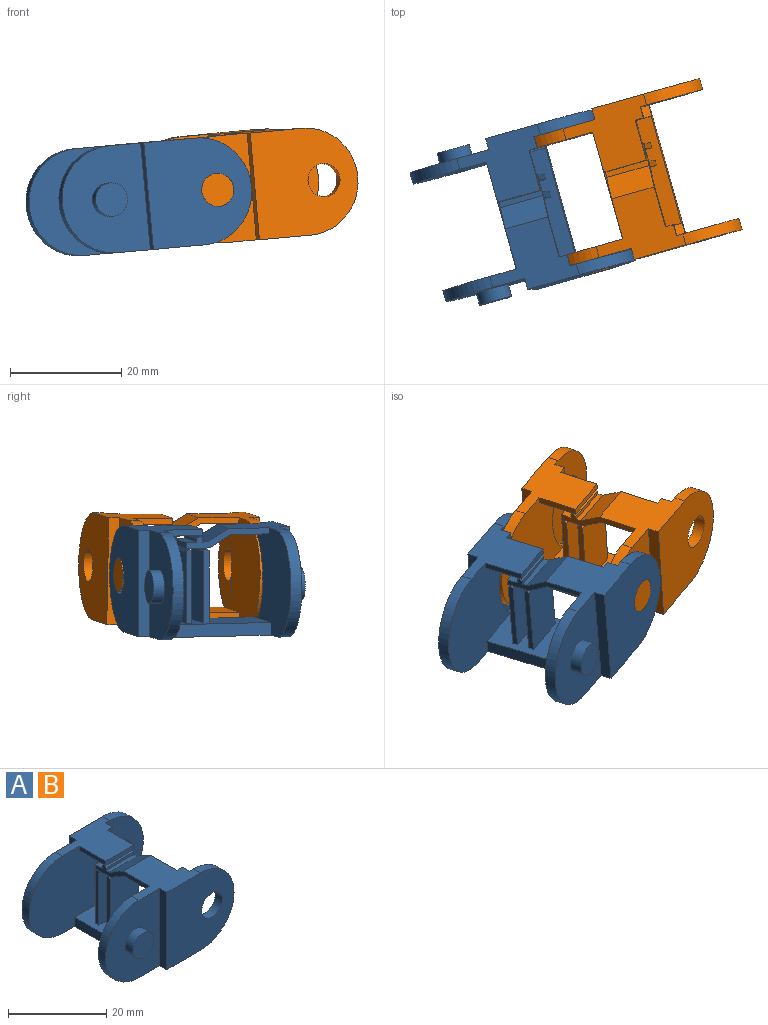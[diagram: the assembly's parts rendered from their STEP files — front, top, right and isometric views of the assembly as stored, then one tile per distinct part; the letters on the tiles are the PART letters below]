
ASSEMBLY  parts=2 mates=1
PART A: 64 faces, bbox 35x28.4x19.3 mm
  f0: plane 8x2mm, normal (0,0,1), area 16mm2, adj f16,f17,f25,f56
  f1: cylinder r=9.65mm len=19.3mm, axis (0,-1,0), area 61.8mm2, adj f3,f6,f14,f43
  f2: cylinder r=3mm len=6mm, axis (0,1,0), area 38.5mm2, adj f14,f43
  f3: plane 28.2x15.7mm, normal (0,0,-1), area 319.2mm2, adj f1,f5,f7,f12,f13,f14,f15,f18
  f4: plane 15.7x11.6mm, normal (0,0,1), area 109.6mm2, adj f5,f7,f13,f15,f16,f17,f27,f29
  f5: plane 24.15x19.3mm, normal (0,1,0), area 326.7mm2, adj f3,f4,f7,f8,f16,f17,f18,f19
  f6: plane 15.7x11.6mm, normal (0,0,1), area 109.6mm2, adj f1,f9,f10,f12,f14,f21,f22,f34
  f7: cylinder r=9.65mm len=19.3mm, axis (0,-1,0), area 62.1mm2, adj f3,f4,f5,f31
  f8: plane 8x7.21mm, normal (0,0,-1), area 57.6mm2, adj f5,f16,f17,f23
  f9: plane 7.52x1.1mm, normal (-1,0,0), area 8.3mm2, adj f6,f11,f21,f22
  f10: plane 7.52x1.1mm, normal (1,0,0), area 8.3mm2, adj f6,f11,f21,f22
  f11: plane 8x7.52mm, normal (0,0,-1), area 60.2mm2, adj f9,f10,f21,f22
  f12: cylinder r=9.65mm len=19.3mm, axis (0,-1,0), area 62.1mm2, adj f3,f6,f21,f35
  f13: cylinder r=9.65mm len=19.3mm, axis (0,-1,0), area 61.8mm2, adj f3,f4,f15,f39
  f14: plane 19.35x19.3mm, normal (0,1,0), area 305.2mm2, adj f1,f2,f3,f6,f34
  f15: plane 19.35x19.3mm, normal (0,-1,0), area 305.2mm2, adj f3,f4,f13,f28,f29
  f16: plane 15.5x3.4mm, normal (-1,0,0), area 18.6mm2, adj f0,f4,f5,f8,f23,f24,f25,f26
  f17: plane 15.5x3.4mm, normal (1,0,0), area 18.6mm2, adj f0,f4,f5,f8,f23,f24,f25,f26
  f18: plane 20x2.3mm, normal (-1,0,0), area 46mm2, adj f3,f5,f19,f21
  f19: plane 20x11mm, normal (0,0,1), area 204mm2, adj f5,f18,f20,f21,f40,f44,f45,f47
  f20: plane 24.12x2.3mm, normal (1,0,0), area 49.7mm2, adj f3,f19,f38,f39,f40,f42,f43,f44
  f21: plane 24.15x19.3mm, normal (0,-1,0), area 326.7mm2, adj f3,f6,f9,f10,f11,f12,f18,f19
  f22: plane 8x1.1mm, normal (0,-1,0.02), area 8.8mm2, adj f6,f9,f10,f11
  f23: plane 8x3.98mm, normal (0,-0.5,-0.87), area 36.8mm2, adj f8,f16,f17,f24
  f24: plane 8x4.31mm, normal (0,0,-1), area 34.5mm2, adj f16,f17,f23,f25
  f25: plane 8x1.09mm, normal (0,1,0), area 8.7mm2, adj f0,f16,f17,f24
  f26: plane 8x0.99mm, normal (0,0.02,1), area 7.9mm2, adj f16,f17,f27,f57
  f27: plane 8x3.97mm, normal (0,0.5,0.87), area 36.7mm2, adj f4,f16,f17,f26
  f28: cylinder r=3mm len=6mm, axis (0,1,0), area 38.5mm2, adj f15,f39
  f29: plane 19.3x2.05mm, normal (-1,0,0), area 39.6mm2, adj f3,f4,f15,f31
  f30: cylinder r=3mm len=6mm, axis (0,1,0), area 41.9mm2, adj f31,f32
  f31: plane 19.3x15.65mm, normal (0,-1,0), area 233.8mm2, adj f3,f4,f7,f29,f30
  f32: plane 6x6mm, normal (0,-1,0.02), area 28.3mm2, adj f30
  f33: cylinder r=3mm len=6mm, axis (0,1,0), area 38.6mm2, adj f35,f36
  f34: plane 19.3x2.05mm, normal (-1,0,0), area 39.6mm2, adj f3,f6,f14,f35
  f35: plane 19.3x15.65mm, normal (0,1,0), area 233.8mm2, adj f3,f6,f12,f33,f34
  f36: plane 6x6mm, normal (0,1,0), area 28.3mm2, adj f33
  f37: plane 2.06x0.89mm, normal (1,0,0), area 1.8mm2, adj f4,f5,f38,f39
  f38: cylinder r=9.85mm len=17.52mm, axis (0,1,0), area 44.5mm2, adj f5,f20,f37,f39,f40
  f39: plane 19.3x16.2mm, normal (0,1,0), area 208.1mm2, adj f3,f4,f13,f20,f28,f37,f38
  f40: plane 2.06x1.41mm, normal (0,-1,0), area 1.6mm2, adj f19,f20,f38
  f41: plane 2.06x0.89mm, normal (1,0,0), area 1.8mm2, adj f6,f21,f42,f43
  f42: cylinder r=9.85mm len=17.52mm, axis (0,-1,0), area 44.5mm2, adj f20,f21,f41,f43,f44
  f43: plane 19.3x16.2mm, normal (0,-1,0), area 208.1mm2, adj f1,f2,f3,f6,f20,f41,f42
  f44: plane 2.06x1.41mm, normal (0,1,0), area 1.6mm2, adj f19,f20,f42
  f45: plane 13.51x1mm, normal (1,0,0), area 13.3mm2, adj f19,f46,f48,f49,f60,f61
  f46: plane 8x0.08mm, normal (0,0.02,1), area 0.7mm2, adj f45,f47,f60,f61
  f47: plane 13.51x1mm, normal (-1,0,0), area 13.3mm2, adj f19,f46,f48,f49,f60,f61
  f48: plane 13.06x8mm, normal (0,-1,0), area 104.5mm2, adj f19,f45,f47,f60
  f49: plane 13.06x8mm, normal (0,1,0), area 104.4mm2, adj f19,f45,f47,f61
  f50: plane 13.46x1mm, normal (-1,0,0), area 13.2mm2, adj f19,f51,f53,f54,f62,f63
  f51: plane 8x0.08mm, normal (0,0.02,1), area 0.7mm2, adj f50,f52,f62,f63
  f52: plane 13.46x1mm, normal (1,0,0), area 13.2mm2, adj f19,f51,f53,f54,f62,f63
  f53: plane 13x8mm, normal (0,1,0), area 104mm2, adj f19,f50,f52,f63
  f54: plane 13x8mm, normal (0,-1,0), area 104mm2, adj f19,f50,f52,f62
  f55: plane 8x0.11mm, normal (0,0.02,1), area 0.9mm2, adj f16,f17,f58,f59
  f56: plane 8x0.63mm, normal (0,1,0), area 5.1mm2, adj f0,f16,f17,f59
  f57: plane 8x0.64mm, normal (0,-1,0.02), area 5.1mm2, adj f16,f17,f26,f58
  f58: plane 8x0.47mm, normal (0,-0.69,0.72), area 5.2mm2, adj f16,f17,f55,f57
  f59: plane 8x0.46mm, normal (0,0.71,0.7), area 5.1mm2, adj f16,f17,f55,f56
  f60: plane 8x0.47mm, normal (0,-0.7,0.71), area 5.2mm2, adj f45,f46,f47,f48
  f61: plane 8x0.46mm, normal (0,0.71,0.7), area 5.1mm2, adj f45,f46,f47,f49
  f62: plane 8x0.47mm, normal (0,-0.7,0.71), area 5.2mm2, adj f50,f51,f52,f54
  f63: plane 8x0.46mm, normal (0,0.71,0.7), area 5.1mm2, adj f50,f51,f52,f53
PART B: same geometry as A
PLACE A rot(axis=(-0.04,-0.31,0.95),16.5deg) t=(-27.2,17.63,26.16)mm
PLACE B rot(axis=(0.02,-0.3,0.95),16.5deg) t=(-8.09,23.2,28.15)mm
MATE revolute B.f32 <-> A.f2  axis (0.27,-0.96,0.02) through (-4.32,9.76,28.35)mm
